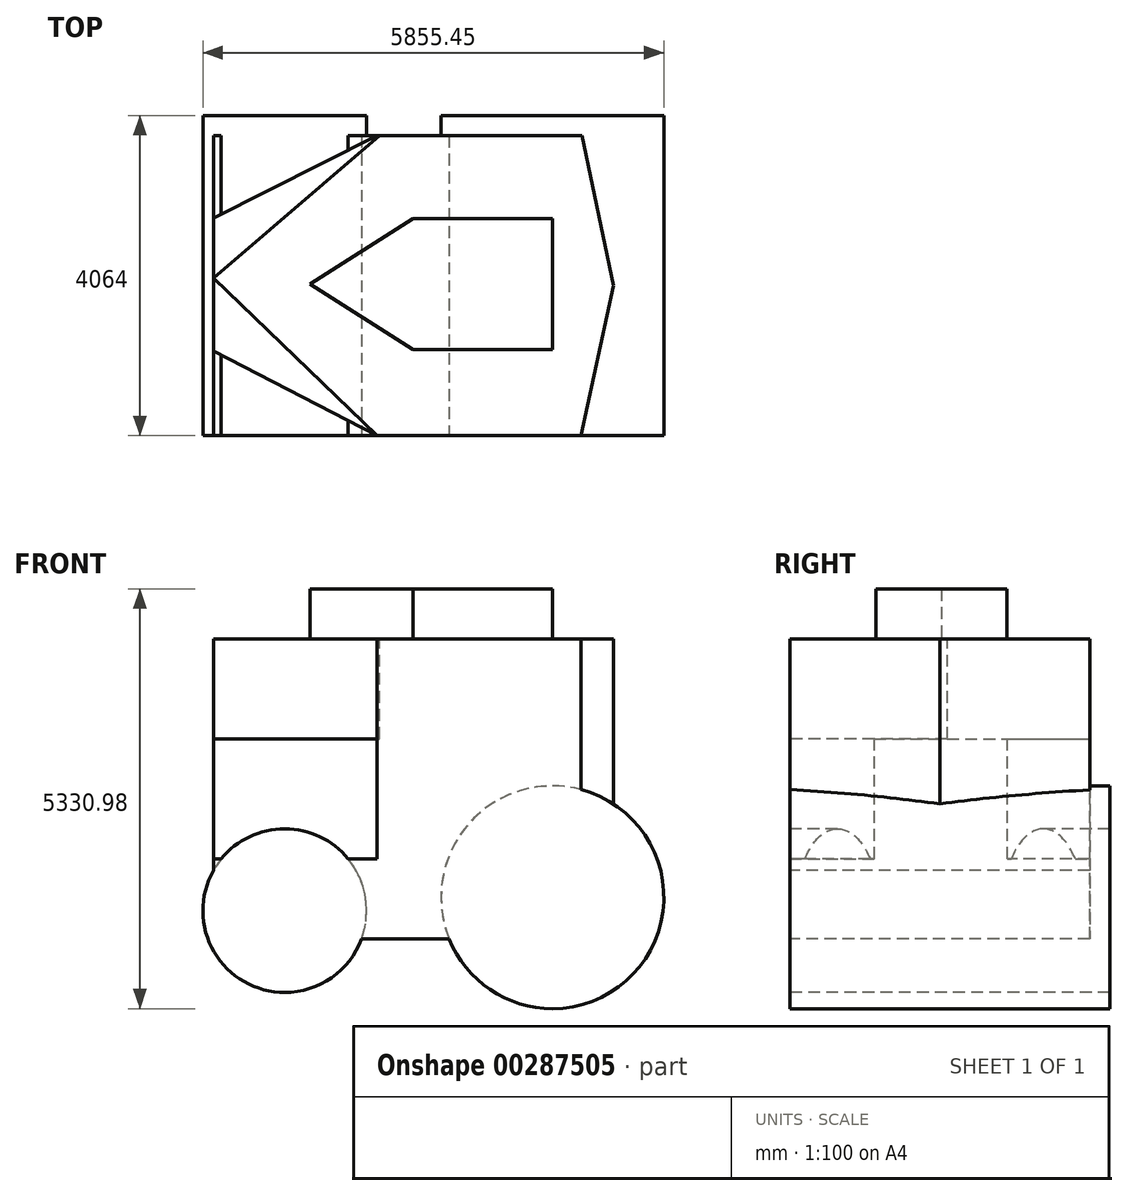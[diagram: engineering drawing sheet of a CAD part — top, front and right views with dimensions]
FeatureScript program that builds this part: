
annotation { "Feature Type Name" : "Feature", "Feature Type Description" : "" }
export const myFeature = defineFeature(function(context is Context, id is Id, definition is map)
    precondition{}
    {
        {
            var Q0;
            Q0=qCreatedBy(makeId("Front.planeOp"),FACE);
            var sketch = newSketch(context, id + "F0", { "sketchPlane" : qUnion([Q0])});
            skLineSegment(sketch, "E0.bottom", {"start": v(-2536.32, 1873.8) * mm, "end": v(2543.68, 1873.8) * mm});
            skLineSegment(sketch, "E0.top", {"start": v(-2536.32, -1936.2) * mm, "end": v(2543.68, -1936.2) * mm});
            skLineSegment(sketch, "E0.left", {"start": v(-2536.32, 1873.8) * mm, "end": v(-2536.32, -1936.2) * mm});
            skLineSegment(sketch, "E0.right", {"start": v(2543.68, 1873.8) * mm, "end": v(2543.68, -1936.2) * mm});
            skSolve(sketch);
        }
        {
            var Q0;
            Q0 = qSketchRegion(id + "F0", true);
            extrude(context, id + "F1", {"entities" : qUnion([Q0]), "depth" : 3810 * mm});
        }
        {
            var Q0;
            Q0=makeQuery(id+"F1.opExtrude","SWEPT_FACE",FACE,{"disambiguationData":[OSD([sQuery(id+"F0.wireOp",EDGE,"E0.bottom")])]});
            var sketch = newSketch(context, id + "F2", { "sketchPlane" : qUnion([Q0])});
            skLineSegment(sketch, "E1", {"start": v(-2536.32, -1811.32) * mm, "end": v(-455.99, -3810) * mm});
            skLineSegment(sketch, "E2", {"start": v(-2536.32, -1811.32) * mm, "end": v(-426.88, 0) * mm});
            skLineSegment(sketch, "E3", {"start": v(-2536.32, -3810) * mm, "end": v(-455.99, -3810) * mm});
            skLineSegment(sketch, "E4", {"start": v(-2536.32, -3810) * mm, "end": v(-2536.32, 0) * mm});
            skLineSegment(sketch, "E5", {"start": v(-2536.32, 0) * mm, "end": v(-426.88, 0) * mm});
            skSolve(sketch);
        }
        {
            var Q0;
            Q0 = qSketchRegion(id + "F2", true);
            extrude(context, id + "F3", {"entities" : qUnion([Q0]), "operationType" : NewBodyOperationType.REMOVE, "oppositeDirection" : true, "depth" : 1270 * mm});
        }
        {
            var Q0;
            Q0=makeQuery(id+"F1.opExtrude","SWEPT_FACE",FACE,{"disambiguationData":[OSD([sQuery(id+"F0.wireOp",EDGE,"E0.bottom")])]});
            var sketch = newSketch(context, id + "F4", { "sketchPlane" : qUnion([Q0])});
            skLineSegment(sketch, "E6", {"start": v(2130.76, -3810) * mm, "end": v(2543.68, -1905) * mm});
            skLineSegment(sketch, "E7", {"start": v(2543.68, -1905) * mm, "end": v(2146.74, 0) * mm});
            skLineSegment(sketch, "E8", {"start": v(2130.76, -3810) * mm, "end": v(2543.68, -3810) * mm});
            skLineSegment(sketch, "E9", {"start": v(2543.68, -3810) * mm, "end": v(2543.68, 0) * mm});
            skLineSegment(sketch, "E10", {"start": v(2543.68, 0) * mm, "end": v(2146.74, 0) * mm});
            skSolve(sketch);
        }
        {
            var Q0;
            Q0 = qSketchRegion(id + "F4", true);
            extrude(context, id + "F5", {"entities" : qUnion([Q0]), "operationType" : NewBodyOperationType.REMOVE, "oppositeDirection" : true, "depth" : 5080 * mm});
        }
        {
            var Q0;
            Q0=makeQuery(id+"F3.boolean.opBoolean","COPY",FACE,{"derivedFrom":makeQuery(id+"F3.opExtrude","CAP_FACE",FACE,{"disambiguationData":[OSD([sQuery(id+"F2.wireOp",EDGE,"E1"),sQuery(id+"F2.wireOp",EDGE,"E3"),sQuery(id+"F2.wireOp",EDGE,"E4")])],"isStart":false})});
            var sketch = newSketch(context, id + "F6", { "sketchPlane" : qUnion([Q0])});
            skLineSegment(sketch, "E11", {"start": v(-2536.32, -2736.48) * mm, "end": v(-455.99, -3810) * mm});
            skLineSegment(sketch, "E12", {"start": v(-455.99, -3810) * mm, "end": v(-2536.32, -3810) * mm});
            skLineSegment(sketch, "E13", {"start": v(-2536.32, -3810) * mm, "end": v(-2536.32, -2736.48) * mm});
            skLineSegment(sketch, "E14", {"start": v(-2536.32, -1047.82) * mm, "end": v(-455.99, 0) * mm});
            skLineSegment(sketch, "E15", {"start": v(-455.99, 0) * mm, "end": v(-2536.32, 0) * mm});
            skLineSegment(sketch, "E16", {"start": v(-2536.32, 0) * mm, "end": v(-2536.32, -1047.82) * mm});
            skSolve(sketch);
        }
        {
            var Q0;
            Q0 = qSketchRegion(id + "F6", true);
            extrude(context, id + "F7", {"entities" : qUnion([Q0]), "operationType" : NewBodyOperationType.REMOVE, "oppositeDirection" : true, "depth" : 1524 * mm});
        }
        {
            var Q0;
            Q0=makeQuery(id+"F1.opExtrude","SWEPT_FACE",FACE,{"disambiguationData":[OSD([sQuery(id+"F0.wireOp",EDGE,"E0.bottom")])]});
            var sketch = newSketch(context, id + "F8", { "sketchPlane" : qUnion([Q0])});
            skLineSegment(sketch, "E17.bottom", {"start": v(0, -2719.28) * mm, "end": v(1768.89, -2719.28) * mm});
            skLineSegment(sketch, "E17.top", {"start": v(0, -1054.64) * mm, "end": v(1768.89, -1054.64) * mm});
            skLineSegment(sketch, "E17.right", {"start": v(1768.89, -2719.28) * mm, "end": v(1768.89, -1054.64) * mm});
            skLineSegment(sketch, "E18", {"start": v(0, -2719.28) * mm, "end": v(-1307.44, -1886.96) * mm});
            skPoint(sketch, "E18.endSnap0", {"position": v(0, -1886.96) * mm});
            skLineSegment(sketch, "E19", {"start": v(-1307.44, -1886.96) * mm, "end": v(0, -1054.64) * mm});
            skSolve(sketch);
        }
        {
            var Q0;
            Q0 = qSketchRegion(id + "F8", true);
            extrude(context, id + "F9", {"entities" : qUnion([Q0]), "operationType" : NewBodyOperationType.ADD, "depth" : 635 * mm});
        }
        {
            var Q0;
            Q0=makeQuery(id+"F1.opExtrude","CAP_FACE",FACE,{"disambiguationData":[OSD([sQuery(id+"F0.wireOp",EDGE,"E0.bottom"),sQuery(id+"F0.wireOp",EDGE,"E0.top"),sQuery(id+"F0.wireOp",EDGE,"E0.left"),sQuery(id+"F0.wireOp",EDGE,"E0.right")])],"isStart":false});
            var sketch = newSketch(context, id + "F10", { "sketchPlane" : qUnion([Q0])});
            skCircle(sketch, "E20", {"center": v(-1629.16, -1576.28) * mm, "radius": 1039.86 * mm});
            skCircle(sketch, "E21", {"center": v(1771.34, -1407.08) * mm, "radius": 1415.1 * mm});
            skSolve(sketch);
        }
        {
            var Q0;
            Q0 = qSketchRegion(id + "F10", true);
            extrude(context, id + "F11", {"entities" : qUnion([Q0]), "operationType" : NewBodyOperationType.ADD, "oppositeDirection" : true, "depth" : 4064 * mm});
        }
    });
